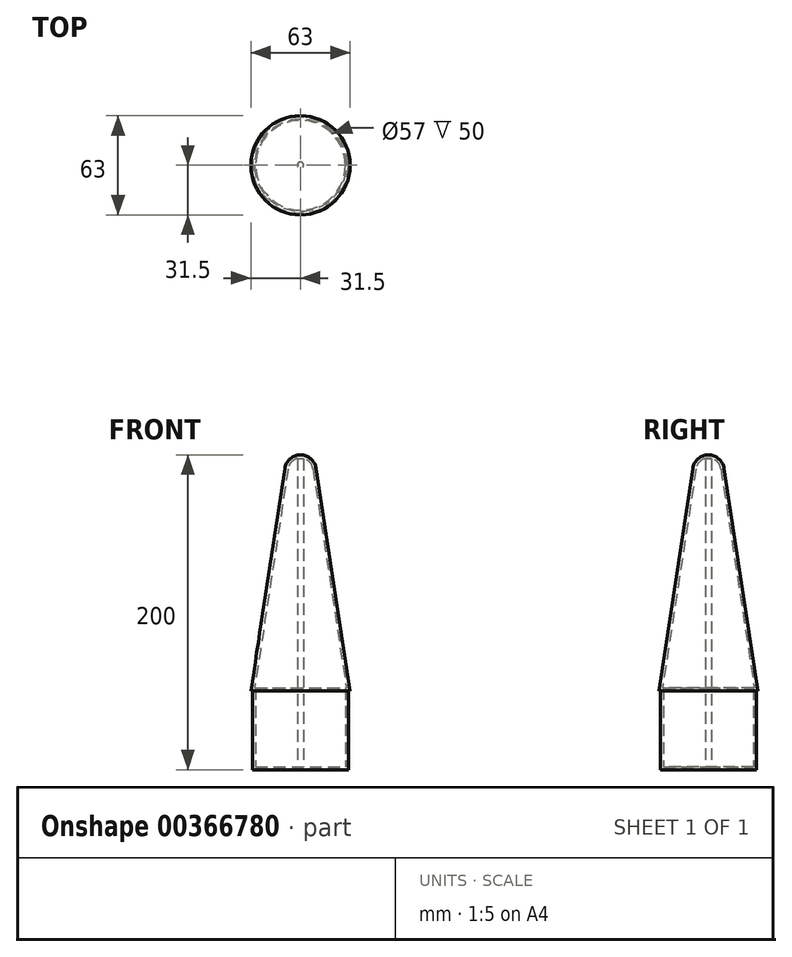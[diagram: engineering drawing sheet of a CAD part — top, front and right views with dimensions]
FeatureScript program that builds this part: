
annotation { "Feature Type Name" : "Feature", "Feature Type Description" : "" }
export const myFeature = defineFeature(function(context is Context, id is Id, definition is map)
    precondition{}
    {
        {
            var Q0;
            Q0=qCreatedBy(makeId("Front.planeOp"),FACE);
            var sketch = newSketch(context, id + "F0", { "sketchPlane" : qUnion([Q0])});
            skLineSegment(sketch, "E0", {"start": v(0, 0) * mm, "end": v(0, 200) * mm});
            skLineSegment(sketch, "E1", {"start": v(0, 0) * mm, "end": v(30.5, 0) * mm});
            skLineSegment(sketch, "E2", {"start": v(30.5, 0) * mm, "end": v(30.5, 50) * mm});
            skLineSegment(sketch, "E3", {"start": v(30.5, 50) * mm, "end": v(31.5, 50) * mm});
            skLineSegment(sketch, "E4", {"start": v(0, 200) * mm, "end": v(0, 190) * mm});
            skArc(sketch, "E5", {"start": v(9.89, 191.5) * mm, "mid": v(6.52, 197.59) * mm, "end": v(0, 200) * mm});
            skLineSegment(sketch, "E6", {"start": v(31.5, 50) * mm, "end": v(9.89, 191.5) * mm});
            skLineSegment(sketch, "E7.0", {"start": v(29.17, 52) * mm, "end": v(7.9, 191.2) * mm});
            skLineSegment(sketch, "E7.1", {"start": v(2, 2) * mm, "end": v(2, 197.75) * mm});
            skLineSegment(sketch, "E7.2", {"start": v(2, 2) * mm, "end": v(28.5, 2) * mm});
            skArc(sketch, "E7.3", {"start": v(7.9, 191.2) * mm, "mid": v(5.94, 195.36) * mm, "end": v(2, 197.75) * mm});
            skLineSegment(sketch, "E7.4", {"start": v(28.5, 2) * mm, "end": v(28.5, 52) * mm});
            skLineSegment(sketch, "E7.5", {"start": v(28.5, 52) * mm, "end": v(29.17, 52) * mm});
            skSolve(sketch);
        }
        {
            var Q0;
            Q0=makeQuery(id+"F0.imprint","IMPRINT",FACE,{"disambiguationData":[TD([[makeQuery(id+"F0.imprint","IMPRINT",EDGE,{"derivedFrom":sQuery(id+"F0.wireOp",EDGE,"E0")}),-1.0]])]});
            var Q1;
            Q1=sQuery(id+"F0.wireOp",EDGE,"E0");
            revolve(context, id + "F1", {"entities" : qUnion([Q0]), "axis" : qUnion([Q1]), "revolveType" : RevolveType.FULL});
        }
    });
